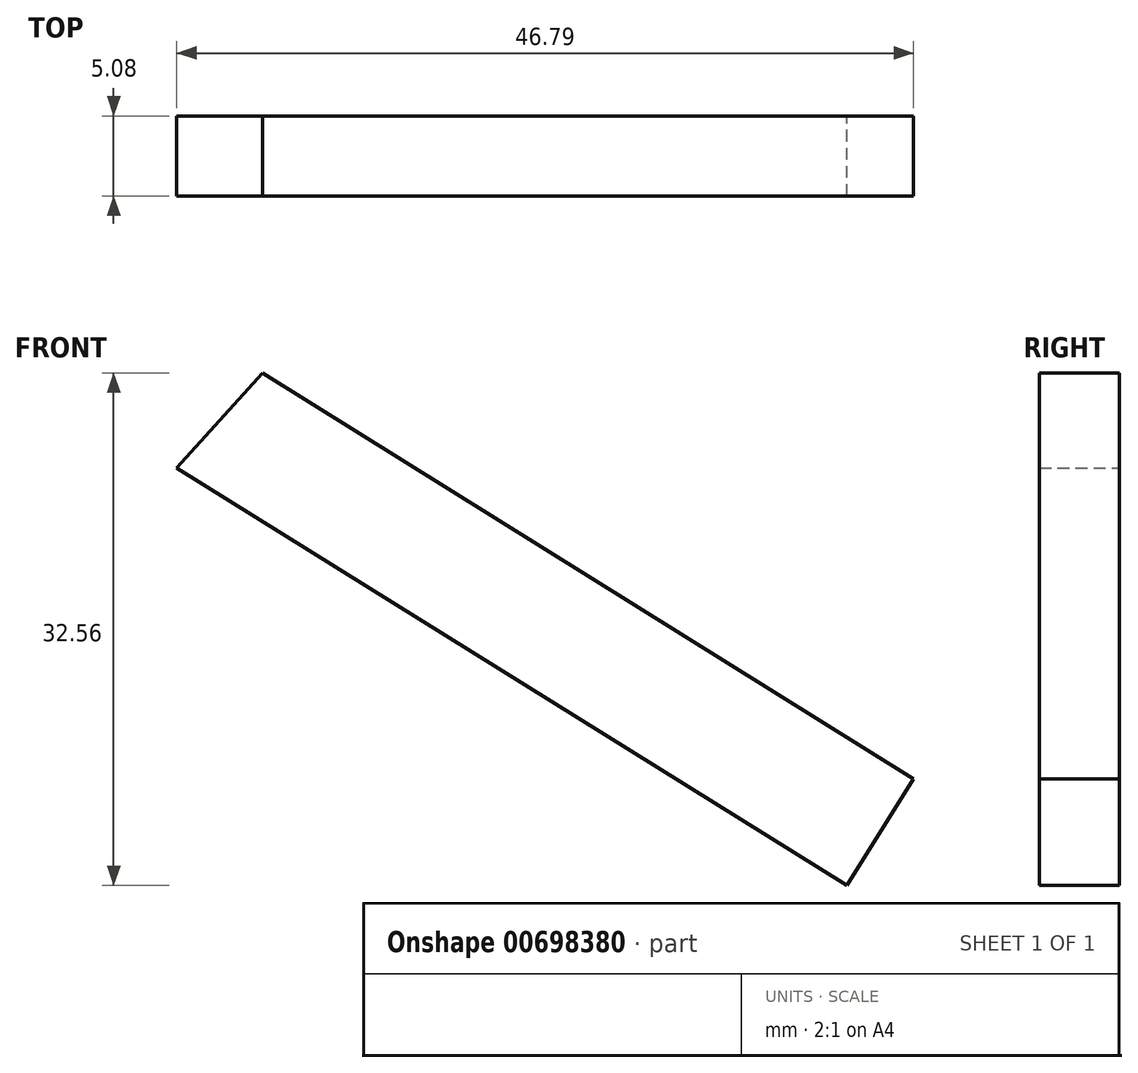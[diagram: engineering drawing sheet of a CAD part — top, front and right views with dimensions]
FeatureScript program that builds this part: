
annotation { "Feature Type Name" : "Feature", "Feature Type Description" : "" }
export const myFeature = defineFeature(function(context is Context, id is Id, definition is map)
    precondition{}
    {
        {
            var Q0;
            Q0=qCreatedBy(makeId("Front.planeOp"),FACE);
            var sketch = newSketch(context, id + "F0", { "sketchPlane" : qUnion([Q0])});
            skLineSegment(sketch, "E0", {"start": v(-24.57, 14.63) * mm, "end": v(16.78, -11.14) * mm});
            skLineSegment(sketch, "E1", {"start": v(16.78, -11.14) * mm, "end": v(12.55, -17.93) * mm});
            skLineSegment(sketch, "E2", {"start": v(12.55, -17.93) * mm, "end": v(-30.01, 8.6) * mm});
            skLineSegment(sketch, "E3", {"start": v(-30.01, 8.6) * mm, "end": v(-24.57, 14.63) * mm});
            skSolve(sketch);
        }
        {
            var Q0;
            Q0=makeQuery(id+"F0.imprint","IMPRINT",FACE,{"disambiguationData":[TD([[makeQuery(id+"F0.imprint","IMPRINT",EDGE,{"derivedFrom":sQuery(id+"F0.wireOp",EDGE,"E0")}),-1.0]])]});
            extrude(context, id + "F1", {"entities" : qUnion([Q0]), "depth" : 5.08 * mm, "offsetDistance" : 25.4 * mm});
        }
    });
